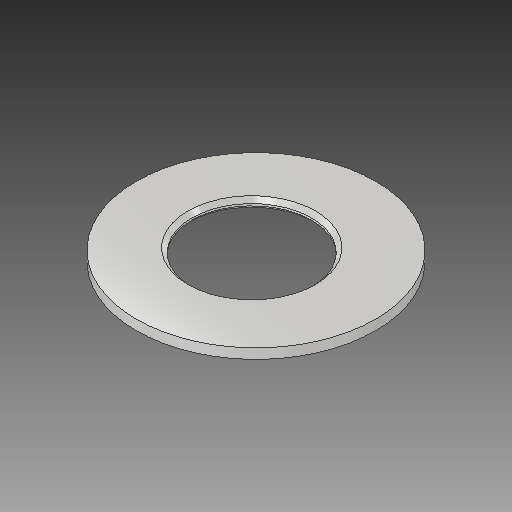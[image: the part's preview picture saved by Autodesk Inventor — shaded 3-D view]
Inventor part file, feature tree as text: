
AUTODESK INVENTOR PART (.ipt)
format: ipt  version: 2019.3 (Build 233278000, 278)  size: 116,736 bytes
history: native  units: mm
features: extrude x1, chamfer x1, sketch x1
ambient origin geometry x8: Origin, YZ Plane, XZ Plane, XY Plane, X Axis, Y Axis, Z Axis, Center Point
bodies: Solid1 (feature_tree)
feature tree (3):
  extrude  "Extrusion1"  Depth=0.5mm
  chamfer  "Chamfer1"  Distance=0.5mm
  sketch  "Sketch1"  dims[d0=6.0mm d1=12.0mm d2=0.5mm d3=0.0mm d4=0.2mm d5=2.0mm d6=45.0deg]
